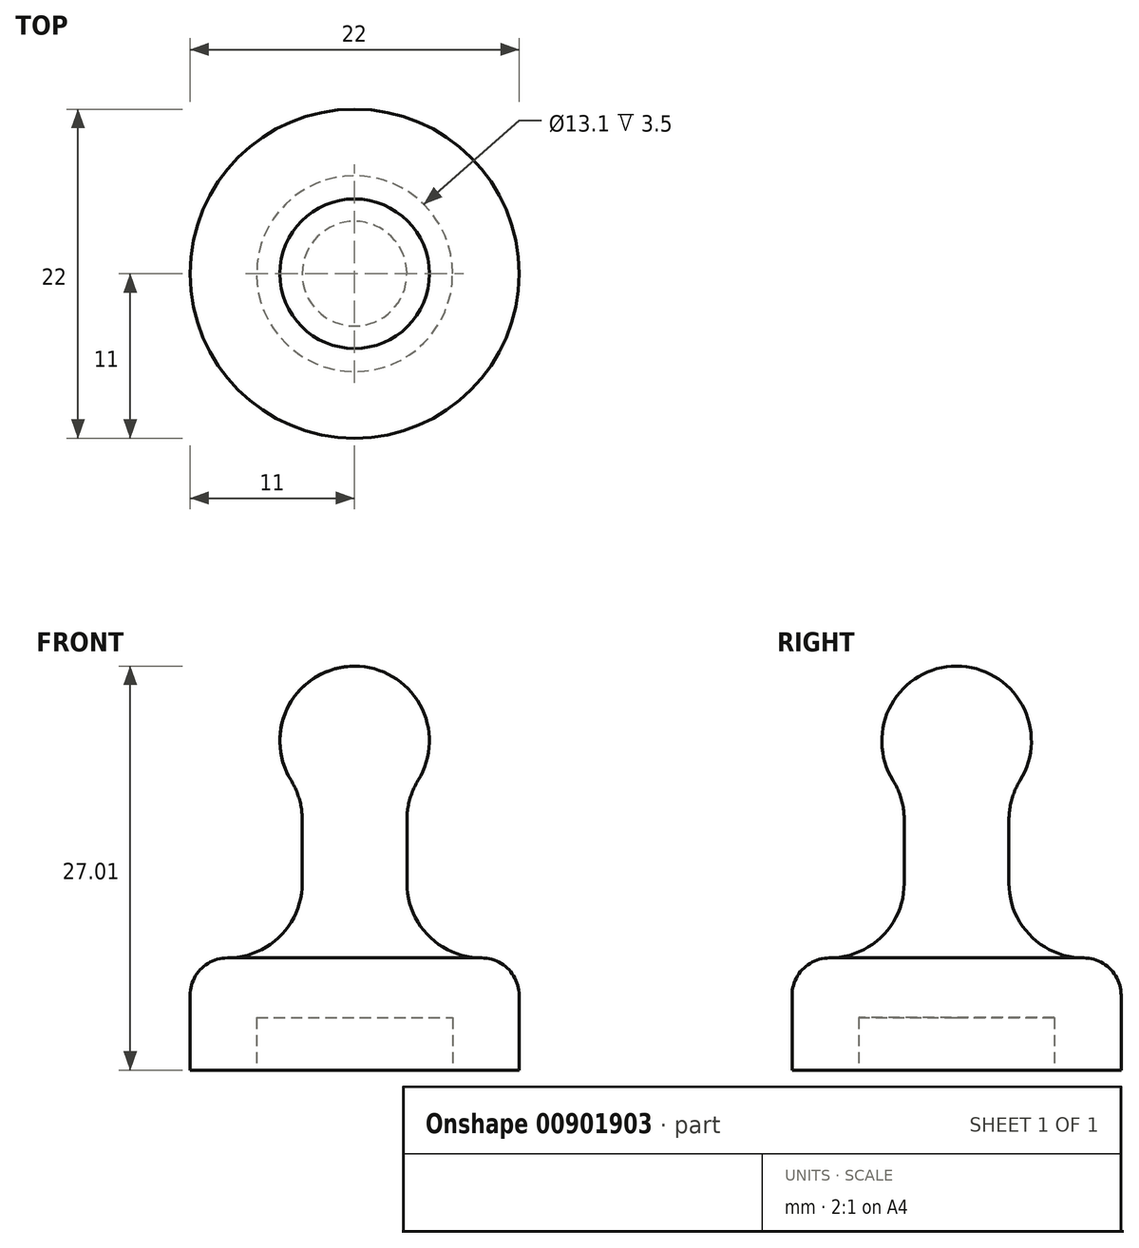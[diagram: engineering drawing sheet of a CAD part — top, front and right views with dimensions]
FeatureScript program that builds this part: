
annotation { "Feature Type Name" : "Feature", "Feature Type Description" : "" }
export const myFeature = defineFeature(function(context is Context, id is Id, definition is map)
    precondition{}
    {
        {
            var Q0;
            Q0=qCreatedBy(makeId("Front.planeOp"),FACE);
            var sketch = newSketch(context, id + "F0", { "sketchPlane" : qUnion([Q0])});
            skLineSegment(sketch, "E0", {"start": v(1, 3.5) * mm, "end": v(1, 27.01) * mm});
            skLineSegment(sketch, "E1", {"start": v(-5.55, 0) * mm, "end": v(-10, 0) * mm});
            skLineSegment(sketch, "E2", {"start": v(-10, 0) * mm, "end": v(-10, 5) * mm});
            skArc(sketch, "E3", {"start": v(1, 27.01) * mm, "mid": v(-3.37, 24.44) * mm, "end": v(-3.25, 19.38) * mm});
            skLineSegment(sketch, "E4", {"start": v(-2.5, 16.74) * mm, "end": v(-2.5, 12.5) * mm});
            skLineSegment(sketch, "E5", {"start": v(-7.5, 7.5) * mm, "end": v(-7.5, 7.5) * mm});
            skPoint(sketch, "E6.visualSharp", {"position": v(-2.5, 18.44) * mm});
            skArc(sketch, "E6.filletArc", {"start": v(-2.5, 16.74) * mm, "mid": v(-2.7, 18.11) * mm, "end": v(-3.25, 19.38) * mm});
            skPoint(sketch, "E7.visualSharp", {"position": v(-2.5, 7.5) * mm});
            skArc(sketch, "E7.filletArc", {"start": v(-7.5, 7.5) * mm, "mid": v(-3.96, 8.96) * mm, "end": v(-2.5, 12.5) * mm});
            skPoint(sketch, "E8.visualSharp", {"position": v(-10, 7.5) * mm});
            skArc(sketch, "E8.filletArc", {"start": v(-7.5, 7.5) * mm, "mid": v(-9.27, 6.77) * mm, "end": v(-10, 5) * mm});
            skLineSegment(sketch, "E9", {"start": v(1, 3.5) * mm, "end": v(-5.55, 3.5) * mm});
            skLineSegment(sketch, "E10", {"start": v(-5.55, 3.5) * mm, "end": v(-5.55, 0) * mm});
            skSolve(sketch);
        }
        {
            var Q0;
            Q0=makeQuery(id+"F0.imprint","IMPRINT",FACE,{"disambiguationData":[TD([[makeQuery(id+"F0.imprint","IMPRINT",EDGE,{"derivedFrom":sQuery(id+"F0.wireOp",EDGE,"E0")}),1.0]])]});
            var Q1;
            Q1=sQuery(id+"F0.wireOp",EDGE,"E0");
            revolve(context, id + "F1", {"surfaceOperationType" : NewSurfaceOperationType.NEW, "entities" : qUnion([Q0]), "axis" : qUnion([Q1]), "revolveType" : RevolveType.FULL});
        }
    });
